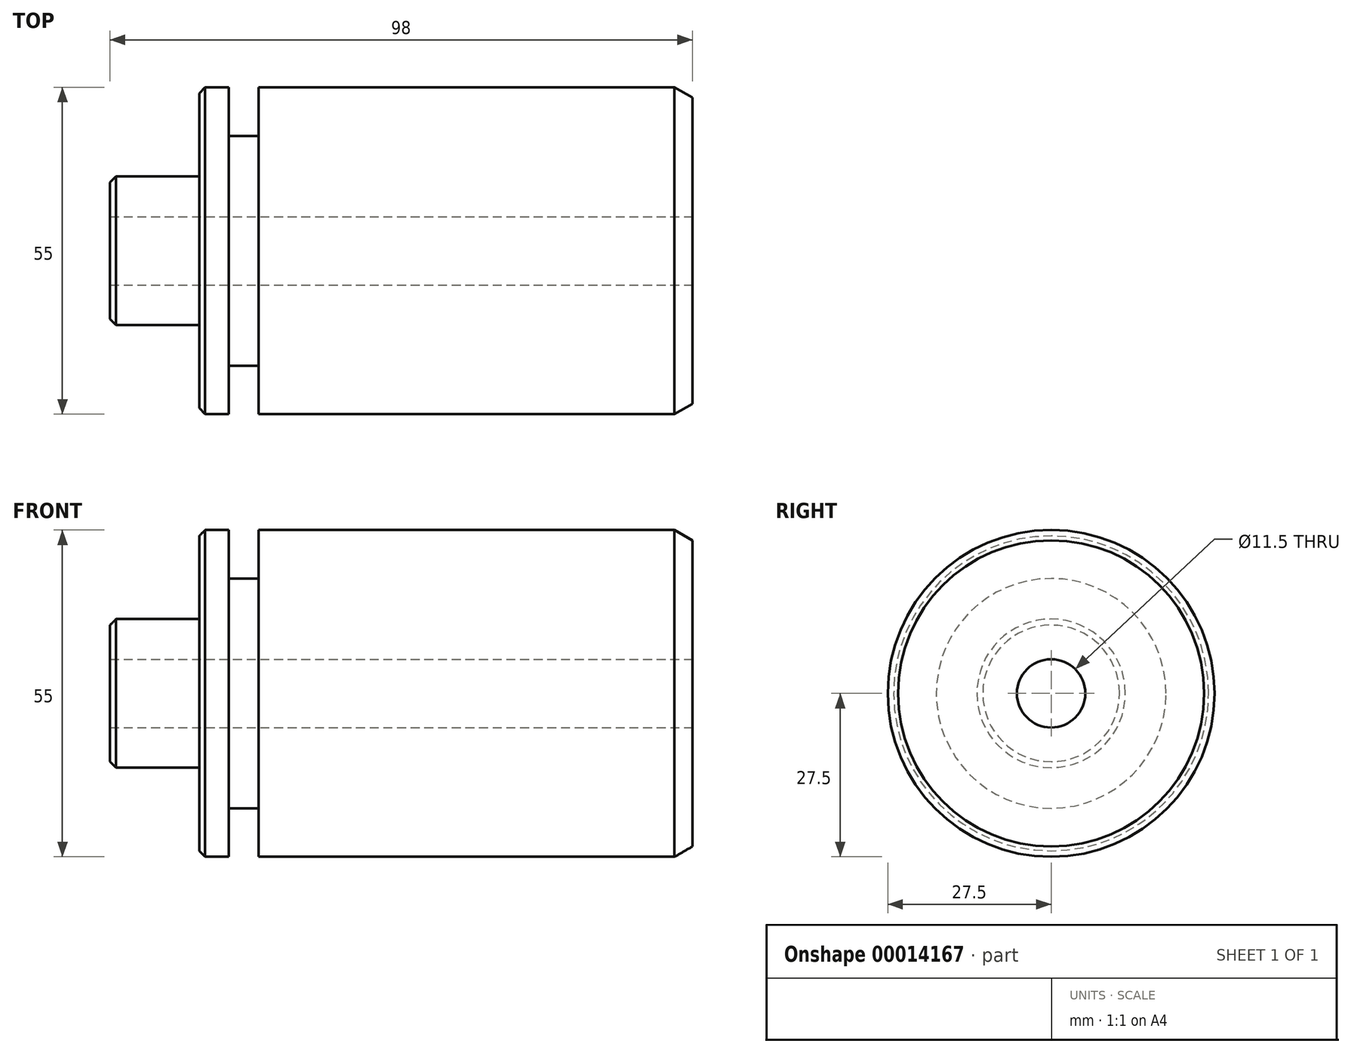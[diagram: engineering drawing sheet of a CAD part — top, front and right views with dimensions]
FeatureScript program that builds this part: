
annotation { "Feature Type Name" : "Feature", "Feature Type Description" : "" }
export const myFeature = defineFeature(function(context is Context, id is Id, definition is map)
    precondition{}
    {
        {
            var Q0;
            Q0=qCreatedBy(makeId("Front.planeOp"),FACE);
            var sketch = newSketch(context, id + "F0", { "sketchPlane" : qUnion([Q0])});
            skLineSegment(sketch, "E0", {"start": v(-135.9, 0) * mm, "end": v(158.07, 0) * mm, "construction": true});
            skLineSegment(sketch, "E1", {"start": v(0, 99.8) * mm, "end": v(0, -101.57) * mm, "construction": true});
            skLineSegment(sketch, "E2.0", {"start": v(-49, 99.8) * mm, "end": v(-49, -101.57) * mm, "construction": true});
            skLineSegment(sketch, "E3", {"start": v(-49, 0) * mm, "end": v(-49, 12.5) * mm});
            skLineSegment(sketch, "E4", {"start": v(-49, 12.5) * mm, "end": v(-34, 12.5) * mm});
            skLineSegment(sketch, "E5", {"start": v(-34, 12.5) * mm, "end": v(-34, 27.5) * mm});
            skLineSegment(sketch, "E6", {"start": v(-34, 27.5) * mm, "end": v(-29, 27.5) * mm});
            skLineSegment(sketch, "E7", {"start": v(-29, 27.5) * mm, "end": v(-29, 19.34) * mm});
            skLineSegment(sketch, "E8", {"start": v(-29, 19.34) * mm, "end": v(-24, 19.34) * mm});
            skLineSegment(sketch, "E9", {"start": v(-24, 19.34) * mm, "end": v(-24, 27.5) * mm});
            skLineSegment(sketch, "E10", {"start": v(-24, 27.5) * mm, "end": v(49, 27.5) * mm});
            skLineSegment(sketch, "E11", {"start": v(49, 27.5) * mm, "end": v(49, 0) * mm});
            skLineSegment(sketch, "E12", {"start": v(-49, 0) * mm, "end": v(49, 0) * mm});
            skSolve(sketch);
        }
        {
            var Q0;
            Q0 = qSketchRegion(id + "F0", true);
            var Q1;
            Q1=sQuery(id+"F0.wireOp",EDGE,"E0");
            revolve(context, id + "F1", {"entities" : qUnion([Q0]), "axis" : qUnion([Q1]), "revolveType" : RevolveType.FULL});
        }
        {
            var Q0;
            Q0=makeQuery(id+"F1.opRevolve","SWEPT_FACE",FACE,{"disambiguationData":[OSD([sQuery(id+"F0.wireOp",EDGE,"E11")])]});
            var sketch = newSketch(context, id + "F2", { "sketchPlane" : qUnion([Q0])});
            skCircle(sketch, "E13", {"center": v(0, 0) * mm, "radius": 5.75 * mm});
            skSolve(sketch);
        }
        {
            var Q0;
            Q0 = qSketchRegion(id + "F2", true);
            extrude(context, id + "F3", {"entities" : qUnion([Q0]), "operationType" : NewBodyOperationType.REMOVE, "endBound" : BoundingType.THROUGH_ALL, "oppositeDirection" : true, "depth" : 25 * mm});
        }
        {
            var Q0;
            Q0=makeQuery(id+"F1.opRevolve","SWEPT_EDGE",EDGE,{"disambiguationData":[OSD([sQuery(id+"F0.wireOp",EDGE,"E10"),sQuery(id+"F0.wireOp",EDGE,"E11")])]});
            chamfer(context, id + "F4", {"entities" : qUnion([Q0]), "chamferType" : ChamferType.OFFSET_ANGLE, "width" : 3 * mm, "oppositeDirection" : false, "angle" : 30 * degree, "tangentPropagation" : true});
        }
        {
            var Q0;
            Q0=makeQuery(id+"F1.opRevolve","SWEPT_EDGE",EDGE,{"disambiguationData":[OSD([sQuery(id+"F0.wireOp",EDGE,"E5"),sQuery(id+"F0.wireOp",EDGE,"E6")])]});
            chamfer(context, id + "F5", {"entities" : qUnion([Q0]), "width" : 1 * mm, "tangentPropagation" : true});
        }
        {
            var Q0;
            Q0=makeQuery(id+"F1.opRevolve","SWEPT_EDGE",EDGE,{"disambiguationData":[OSD([sQuery(id+"F0.wireOp",EDGE,"E3"),sQuery(id+"F0.wireOp",EDGE,"E4")])]});
            chamfer(context, id + "F6", {"entities" : qUnion([Q0]), "width" : 1 * mm, "tangentPropagation" : true});
        }
    });
